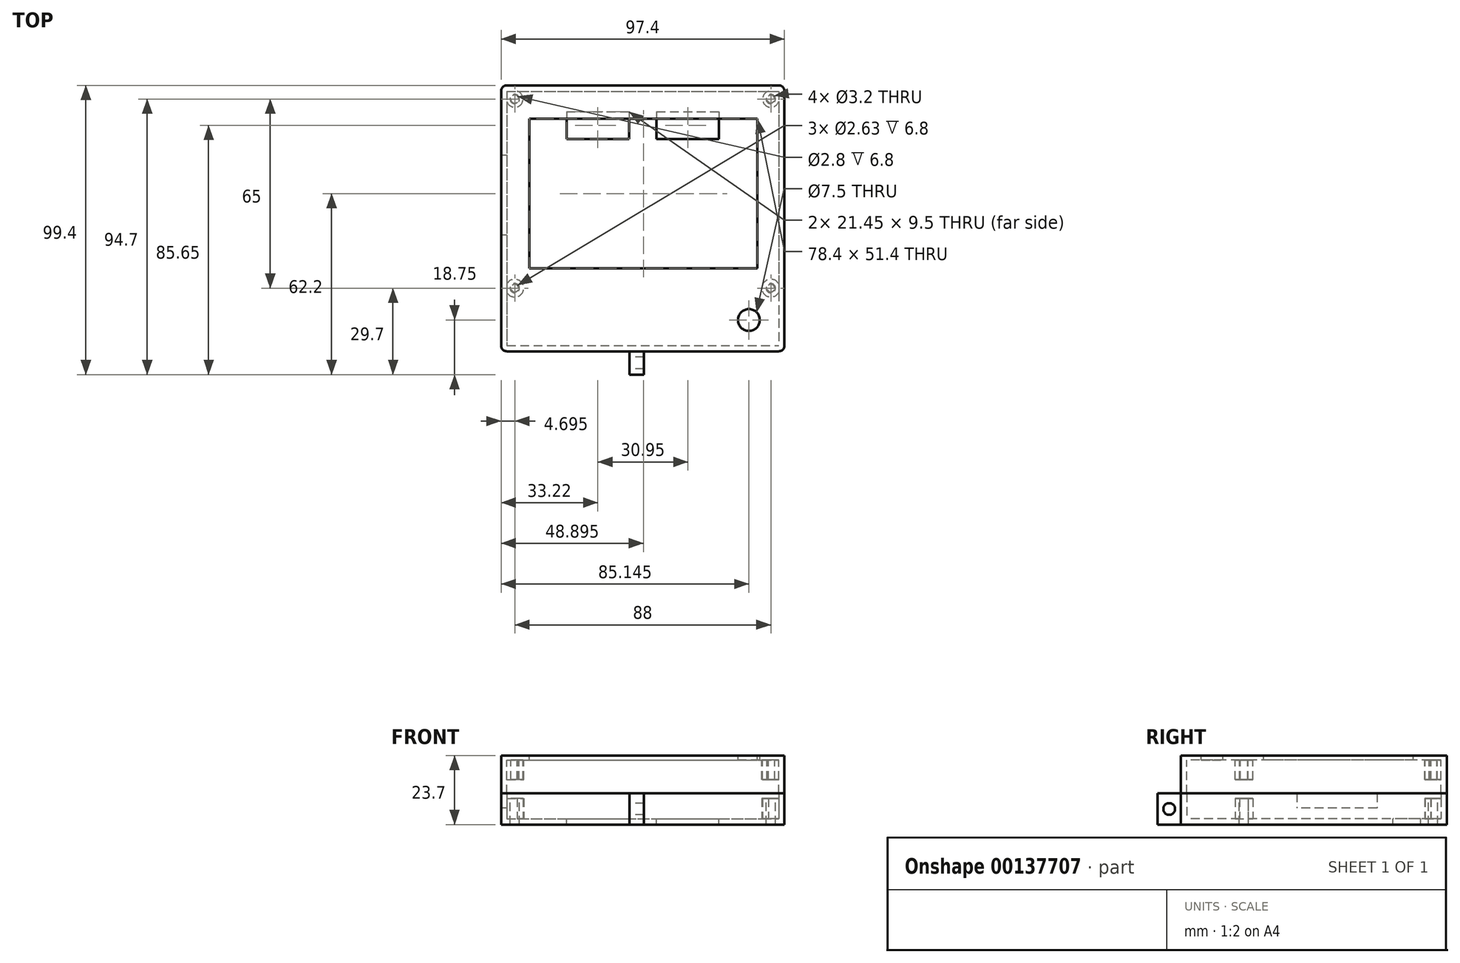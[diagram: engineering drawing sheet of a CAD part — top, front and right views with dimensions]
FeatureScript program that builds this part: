
annotation { "Feature Type Name" : "Feature", "Feature Type Description" : "" }
export const myFeature = defineFeature(function(context is Context, id is Id, definition is map)
    precondition{}
    {
        {
            var Q0;
            Q0=qCreatedBy(makeId("Top.planeOp"),FACE);
            var sketch = newSketch(context, id + "F0", { "sketchPlane" : qUnion([Q0])});
            skLineSegment(sketch, "E0.bottom", {"start": v(-44.61, 43.7) * mm, "end": v(48.79, 43.7) * mm});
            skLineSegment(sketch, "E0.top", {"start": v(-44.61, -43.7) * mm, "end": v(48.79, -43.7) * mm});
            skLineSegment(sketch, "E0.left", {"start": v(-44.61, 43.7) * mm, "end": v(-44.61, -43.7) * mm});
            skLineSegment(sketch, "E0.right", {"start": v(48.79, 43.7) * mm, "end": v(48.79, -43.7) * mm});
            skPoint(sketch, "E0.middle", {"position": v(2.09, 0) * mm});
            skLineSegment(sketch, "E1", {"start": v(-24.11, 36.7) * mm, "end": v(-2.66, 36.7) * mm});
            skLineSegment(sketch, "E2.0", {"start": v(-24.11, 27.2) * mm, "end": v(-2.66, 27.2) * mm});
            skLineSegment(sketch, "E3", {"start": v(-24.11, 36.7) * mm, "end": v(-24.11, 27.2) * mm});
            skLineSegment(sketch, "E4", {"start": v(-2.66, 36.7) * mm, "end": v(-2.66, 27.2) * mm});
            skLineSegment(sketch, "E5", {"start": v(6.84, 36.7) * mm, "end": v(6.84, 27.2) * mm});
            skLineSegment(sketch, "E6", {"start": v(28.29, 36.7) * mm, "end": v(28.29, 27.2) * mm});
            skLineSegment(sketch, "E7.trimOffspring", {"start": v(6.84, 36.7) * mm, "end": v(28.29, 36.7) * mm});
            skLineSegment(sketch, "E8.trimOffspring", {"start": v(6.84, 27.2) * mm, "end": v(28.29, 27.2) * mm});
            skCircle(sketch, "E9", {"center": v(-41.91, 41) * mm, "radius": 1.6 * mm});
            skCircle(sketch, "E10", {"center": v(-41.91, -24) * mm, "radius": 1.6 * mm});
            skCircle(sketch, "E11", {"center": v(46.09, -24) * mm, "radius": 1.6 * mm});
            skCircle(sketch, "E12", {"center": v(46.09, 41) * mm, "radius": 1.6 * mm});
            skLineSegment(sketch, "E13.0", {"start": v(-46.61, 45.7) * mm, "end": v(-46.61, -45.7) * mm});
            skLineSegment(sketch, "E13.1", {"start": v(-46.61, 45.7) * mm, "end": v(50.79, 45.7) * mm});
            skLineSegment(sketch, "E13.2", {"start": v(50.79, 45.7) * mm, "end": v(50.79, -45.7) * mm});
            skLineSegment(sketch, "E13.3", {"start": v(-46.61, -45.7) * mm, "end": v(-2.5, -45.7) * mm});
            skArc(sketch, "E14", {"start": v(-44.61, -25.46) * mm, "mid": v(-38.85, -24) * mm, "end": v(-44.61, -22.54) * mm});
            skArc(sketch, "E15", {"start": v(48.79, -22.54) * mm, "mid": v(43.02, -24) * mm, "end": v(48.79, -25.46) * mm});
            skArc(sketch, "E16.trimOffspring", {"start": v(45.31, 43.7) * mm, "mid": v(44.1, 39.01) * mm, "end": v(48.79, 40.23) * mm});
            skArc(sketch, "E17.trimOffspring", {"start": v(-44.61, 40.15) * mm, "mid": v(-39.91, 39) * mm, "end": v(-41.06, 43.7) * mm});
            skLineSegment(sketch, "E18", {"start": v(0, -61.1) * mm, "end": v(0, -49.71) * mm, "construction": true});
            skLineSegment(sketch, "E19", {"start": v(-2.5, -45.7) * mm, "end": v(-2.5, -53.7) * mm});
            skLineSegment(sketch, "E20", {"start": v(-2.5, -53.7) * mm, "end": v(0, -53.7) * mm});
            skLineSegment(sketch, "E21.MirrorCS", {"start": v(2.5, -53.7) * mm, "end": v(0, -53.7) * mm});
            skLineSegment(sketch, "E22.MirrorCS", {"start": v(2.5, -45.7) * mm, "end": v(2.5, -53.7) * mm});
            skLineSegment(sketch, "E23.trimOffspring", {"start": v(2.5, -45.7) * mm, "end": v(50.79, -45.7) * mm});
            skLineSegment(sketch, "E24", {"start": v(-2.5, -45.7) * mm, "end": v(2.5, -45.7) * mm});
            skSolve(sketch);
        }
        {
            var Q0;
            Q0=makeQuery(id+"F0.imprint","IMPRINT",FACE,{"disambiguationData":[TD([[makeQuery(id+"F0.imprint","IMPRINT",EDGE,{"derivedFrom":sQuery(id+"F0.wireOp",EDGE,"E0.bottom")}),-1.0]])]});
            var Q1;
            Q1=makeQuery(id+"F0.imprint","IMPRINT",FACE,{"disambiguationData":[TD([[makeQuery(id+"F0.imprint","IMPRINT",EDGE,{"derivedFrom":sQuery(id+"F0.wireOp",EDGE,"E0.bottom")}),1.0]])]});
            var Q2;
            {var subQ1=sQuery(id+"F0.wireOp",EDGE,"E0.top");Q2=makeQuery(id+"F0.imprint","IMPRINT",FACE,{"disambiguationData":[TD([[makeQuery(id+"F0.imprint","IMPRINT",EDGE,{"derivedFrom":subQ1}),1.0]])]});}
            var Q3;
            Q3=makeQuery(id+"F0.imprint","IMPRINT",FACE,{"disambiguationData":[TD([[makeQuery(id+"F0.imprint","IMPRINT",EDGE,{"derivedFrom":sQuery(id+"F0.wireOp",EDGE,"E10")}),-1.0]])]});
            var Q4;
            Q4=makeQuery(id+"F0.imprint","IMPRINT",FACE,{"disambiguationData":[TD([[makeQuery(id+"F0.imprint","IMPRINT",EDGE,{"derivedFrom":sQuery(id+"F0.wireOp",EDGE,"E11")}),-1.0]])]});
            var Q5;
            Q5=makeQuery(id+"F0.imprint","IMPRINT",FACE,{"disambiguationData":[TD([[makeQuery(id+"F0.imprint","IMPRINT",EDGE,{"derivedFrom":sQuery(id+"F0.wireOp",EDGE,"E19")}),1.0]])]});
            extrude(context, id + "F1", {"entities" : qUnion([Q0, Q1, Q2, Q3, Q4, Q5]), "oppositeDirection" : true, "depth" : 2 * mm});
        }
        {
            var Q0;
            Q0=makeQuery(id+"F0.imprint","IMPRINT",FACE,{"disambiguationData":[TD([[makeQuery(id+"F0.imprint","IMPRINT",EDGE,{"derivedFrom":sQuery(id+"F0.wireOp",EDGE,"E9")}),-1.0]])]});
            var Q1;
            Q1=makeQuery(id+"F0.imprint","IMPRINT",FACE,{"disambiguationData":[TD([[makeQuery(id+"F0.imprint","IMPRINT",EDGE,{"derivedFrom":sQuery(id+"F0.wireOp",EDGE,"E12")}),-1.0]])]});
            var Q2;
            Q2=makeQuery(id+"F0.imprint","IMPRINT",FACE,{"disambiguationData":[TD([[makeQuery(id+"F0.imprint","IMPRINT",EDGE,{"derivedFrom":sQuery(id+"F0.wireOp",EDGE,"E11")}),-1.0]])]});
            var Q3;
            Q3=makeQuery(id+"F0.imprint","IMPRINT",FACE,{"disambiguationData":[TD([[makeQuery(id+"F0.imprint","IMPRINT",EDGE,{"derivedFrom":sQuery(id+"F0.wireOp",EDGE,"E10")}),-1.0]])]});
            extrude(context, id + "F2", {"entities" : qUnion([Q0, Q1, Q2, Q3]), "operationType" : NewBodyOperationType.ADD, "depth" : 7 * mm});
        }
        {
            var Q0;
            {var subQ1=sQuery(id+"F0.wireOp",EDGE,"E0.top");Q0=makeQuery(id+"F0.imprint","IMPRINT",FACE,{"disambiguationData":[TD([[makeQuery(id+"F0.imprint","IMPRINT",EDGE,{"derivedFrom":subQ1}),-1.0]])]});}
            var Q1;
            Q1=makeQuery(id+"F0.imprint","IMPRINT",FACE,{"disambiguationData":[TD([[makeQuery(id+"F0.imprint","IMPRINT",EDGE,{"derivedFrom":sQuery(id+"F0.wireOp",EDGE,"E19")}),1.0]])]});
            extrude(context, id + "F3", {"entities" : qUnion([Q0, Q1]), "operationType" : NewBodyOperationType.ADD, "depth" : 8.7 * mm});
        }
        {
            var Q0;
            {var subQ0=sQuery(id+"F0.wireOp",EDGE,"E13.0");Q0=makeQuery(id+"F3.boolean.opBoolean","MERGE",FACE,{"derivedFrom":[makeQuery(id+"F1.opExtrude","SWEPT_FACE",FACE,{"disambiguationData":[OSD([subQ0])]}),makeQuery(id+"F3.opExtrude","SWEPT_FACE",FACE,{"disambiguationData":[OSD([subQ0])]})]});}
            var sketch = newSketch(context, id + "F4", { "sketchPlane" : qUnion([Q0])});
            skLineSegment(sketch, "E25.0", {"start": v(-43.7, 8.7) * mm, "end": v(-43.7, 7) * mm, "construction": true});
            skLineSegment(sketch, "E26.0", {"start": v(-43.7, 7) * mm, "end": v(-40.15, 7) * mm, "construction": true});
            skLineSegment(sketch, "E27", {"start": v(-21.7, 3.7) * mm, "end": v(5.8, 3.7) * mm});
            skLineSegment(sketch, "E28", {"start": v(-21.7, 12.56) * mm, "end": v(-21.7, 3.7) * mm});
            skLineSegment(sketch, "E29", {"start": v(5.8, 13.27) * mm, "end": v(5.8, 3.7) * mm});
            skPoint(sketch, "E30.orphan", {"position": v(-21.7, 1.97) * mm});
            skPoint(sketch, "E31.orphan", {"position": v(5.8, 1.97) * mm});
            skSolve(sketch);
        }
        {
            var Q0;
            {var subQ0=sQuery(id+"F4.wireOp",EDGE,"E27");Q0=makeQuery(id+"F4.imprint","IMPRINT",FACE,{"disambiguationData":[TD([[makeQuery(id+"F4.imprint","IMPRINT",EDGE,{"derivedFrom":subQ0}),1.0]])]});}
            extrude(context, id + "F5", {"entities" : qUnion([Q0]), "operationType" : NewBodyOperationType.REMOVE, "endBound" : BoundingType.UP_TO_NEXT, "oppositeDirection" : true, "depth" : 25 * mm});
        }
        {
            var Q0;
            Q0=makeQuery(id+"F3.opExtrude","CAP_FACE",FACE,{"disambiguationData":[OSD([sQuery(id+"F0.wireOp",EDGE,"E0.bottom"),sQuery(id+"F0.wireOp",EDGE,"E0.top"),sQuery(id+"F0.wireOp",EDGE,"E0.left"),sQuery(id+"F0.wireOp",EDGE,"E0.right"),sQuery(id+"F0.wireOp",EDGE,"E13.0"),sQuery(id+"F0.wireOp",EDGE,"E13.1"),sQuery(id+"F0.wireOp",EDGE,"E13.2"),sQuery(id+"F0.wireOp",EDGE,"E13.3")])],"isStart":false});
            cPlane(context, id + "F6", {"entities" : qUnion([Q0]), "cplaneType" : CPlaneType.OFFSET, "offset" : 13 * mm, "width" : 150 * mm, "height" : 150 * mm});
        }
        {
            var Q0;
            Q0=qCreatedBy(id+"F6.planeOp",FACE);
            var sketch = newSketch(context, id + "F7", { "sketchPlane" : qUnion([Q0])});
            skPoint(sketch, "E32.0", {"position": v(46.09, -24) * mm});
            skLineSegment(sketch, "E33.0", {"start": v(-46.61, 45.7) * mm, "end": v(-46.61, -45.7) * mm});
            skLineSegment(sketch, "E34.0", {"start": v(-46.61, 45.7) * mm, "end": v(50.79, 45.7) * mm});
            skLineSegment(sketch, "E35.0", {"start": v(50.79, 45.7) * mm, "end": v(50.79, -45.7) * mm});
            skLineSegment(sketch, "E36.0", {"start": v(-46.61, -45.7) * mm, "end": v(-2.5, -45.7) * mm});
            skLineSegment(sketch, "E37.0", {"start": v(-44.61, 43.7) * mm, "end": v(-44.61, -43.7) * mm});
            skLineSegment(sketch, "E38.0", {"start": v(-44.61, 43.7) * mm, "end": v(48.79, 43.7) * mm});
            skLineSegment(sketch, "E39.0", {"start": v(48.79, 43.7) * mm, "end": v(48.79, -43.7) * mm});
            skLineSegment(sketch, "E40.0", {"start": v(-44.61, -43.7) * mm, "end": v(48.79, -43.7) * mm});
            skArc(sketch, "E41.0", {"start": v(-44.61, 40.15) * mm, "mid": v(-39.91, 39) * mm, "end": v(-41.06, 43.7) * mm});
            skArc(sketch, "E42.0", {"start": v(45.31, 43.7) * mm, "mid": v(44.1, 39.01) * mm, "end": v(48.79, 40.23) * mm});
            skArc(sketch, "E43.0", {"start": v(-44.61, -25.46) * mm, "mid": v(-38.85, -24) * mm, "end": v(-44.61, -22.54) * mm});
            skArc(sketch, "E44.0", {"start": v(48.79, -22.54) * mm, "mid": v(43.02, -24) * mm, "end": v(48.79, -25.46) * mm});
            skLineSegment(sketch, "E45.bottom", {"start": v(-36.91, 34.2) * mm, "end": v(41.49, 34.2) * mm});
            skLineSegment(sketch, "E45.top", {"start": v(-36.91, -17.2) * mm, "end": v(41.49, -17.2) * mm});
            skLineSegment(sketch, "E45.left", {"start": v(-36.91, 34.2) * mm, "end": v(-36.91, -17.2) * mm});
            skLineSegment(sketch, "E45.right", {"start": v(41.49, 34.2) * mm, "end": v(41.49, -17.2) * mm});
            skCircle(sketch, "E46", {"center": v(-41.91, 41) * mm, "radius": 1.4 * mm});
            skCircle(sketch, "E47", {"center": v(46.09, 41) * mm, "radius": 1.31 * mm});
            skCircle(sketch, "E48", {"center": v(-41.91, -24) * mm, "radius": 1.31 * mm});
            skCircle(sketch, "E49", {"center": v(46.09, -24) * mm, "radius": 1.31 * mm});
            skCircle(sketch, "E50", {"center": v(38.54, -34.95) * mm, "radius": 3.75 * mm});
            skLineSegment(sketch, "E51.0", {"start": v(2.5, -45.7) * mm, "end": v(50.79, -45.7) * mm});
            skLineSegment(sketch, "E52.0", {"start": v(-2.5, -45.7) * mm, "end": v(2.5, -45.7) * mm});
            skSolve(sketch);
        }
        {
            var Q0;
            Q0=makeQuery(id+"F7.imprint","IMPRINT",FACE,{"disambiguationData":[TD([[makeQuery(id+"F7.imprint","IMPRINT",EDGE,{"derivedFrom":sQuery(id+"F7.wireOp",EDGE,"E33.0")}),1.0]])]});
            extrude(context, id + "F8", {"entities" : qUnion([Q0]), "oppositeDirection" : true, "depth" : 13 * mm});
        }
        {
            var Q0;
            {var subQ3=sQuery(id+"F7.wireOp",EDGE,"E41.0");Q0=makeQuery(id+"F7.imprint","IMPRINT",FACE,{"disambiguationData":[TD([[makeQuery(id+"F7.imprint","IMPRINT",EDGE,{"derivedFrom":subQ3}),1.0]])]});}
            var Q1;
            {var subQ3=sQuery(id+"F7.wireOp",EDGE,"E42.0");Q1=makeQuery(id+"F7.imprint","IMPRINT",FACE,{"disambiguationData":[TD([[makeQuery(id+"F7.imprint","IMPRINT",EDGE,{"derivedFrom":subQ3}),1.0]])]});}
            var Q2;
            {var subQ0=sQuery(id+"F7.wireOp",EDGE,"E44.0");Q2=makeQuery(id+"F7.imprint","IMPRINT",FACE,{"disambiguationData":[TD([[makeQuery(id+"F7.imprint","IMPRINT",EDGE,{"derivedFrom":subQ0}),1.0]])]});}
            var Q3;
            {var subQ0=sQuery(id+"F7.wireOp",EDGE,"E43.0");Q3=makeQuery(id+"F7.imprint","IMPRINT",FACE,{"disambiguationData":[TD([[makeQuery(id+"F7.imprint","IMPRINT",EDGE,{"derivedFrom":subQ0}),1.0]])]});}
            extrude(context, id + "F9", {"entities" : qUnion([Q0, Q1, Q2, Q3]), "operationType" : NewBodyOperationType.ADD, "oppositeDirection" : true, "depth" : 8.3 * mm});
        }
        {
            var Q0;
            {var subQ2=sQuery(id+"F7.wireOp",EDGE,"E40.0");Q0=makeQuery(id+"F7.imprint","IMPRINT",FACE,{"disambiguationData":[TD([[makeQuery(id+"F7.imprint","IMPRINT",EDGE,{"derivedFrom":subQ2}),1.0]])]});}
            var Q1;
            Q1=makeQuery(id+"F7.imprint","IMPRINT",FACE,{"disambiguationData":[TD([[makeQuery(id+"F7.imprint","IMPRINT",EDGE,{"derivedFrom":sQuery(id+"F7.wireOp",EDGE,"E46")}),1.0]])]});
            var Q2;
            Q2=makeQuery(id+"F7.imprint","IMPRINT",FACE,{"disambiguationData":[TD([[makeQuery(id+"F7.imprint","IMPRINT",EDGE,{"derivedFrom":sQuery(id+"F7.wireOp",EDGE,"E48")}),1.0]])]});
            var Q3;
            Q3=makeQuery(id+"F7.imprint","IMPRINT",FACE,{"disambiguationData":[TD([[makeQuery(id+"F7.imprint","IMPRINT",EDGE,{"derivedFrom":sQuery(id+"F7.wireOp",EDGE,"E47")}),1.0]])]});
            var Q4;
            Q4=makeQuery(id+"F7.imprint","IMPRINT",FACE,{"disambiguationData":[TD([[makeQuery(id+"F7.imprint","IMPRINT",EDGE,{"derivedFrom":sQuery(id+"F7.wireOp",EDGE,"E49")}),1.0]])]});
            extrude(context, id + "F10", {"entities" : qUnion([Q0, Q1, Q2, Q3, Q4]), "operationType" : NewBodyOperationType.ADD, "oppositeDirection" : true, "depth" : 1.5 * mm});
        }
        {
            var Q0;
            {var subQ0=sQuery(id+"F0.wireOp",EDGE,"E19");Q0=makeQuery(id+"F3.boolean.opBoolean","MERGE",FACE,{"derivedFrom":[makeQuery(id+"F1.opExtrude","SWEPT_FACE",FACE,{"disambiguationData":[OSD([subQ0])]}),makeQuery(id+"F3.opExtrude","SWEPT_FACE",FACE,{"disambiguationData":[OSD([subQ0])]})]});}
            var sketch = newSketch(context, id + "F11", { "sketchPlane" : qUnion([Q0])});
            skCircle(sketch, "E53", {"center": v(49.7, 3.35) * mm, "radius": 2 * mm});
            skPoint(sketch, "E53.centerSnap0", {"position": v(53.7, 3.35) * mm});
            skPoint(sketch, "E53.centerSnap1", {"position": v(49.7, 8.7) * mm});
            skSolve(sketch);
        }
        {
            var Q0;
            Q0=makeQuery(id+"F11.imprint","IMPRINT",FACE,{"disambiguationData":[TD([[makeQuery(id+"F11.imprint","IMPRINT",EDGE,{"derivedFrom":sQuery(id+"F11.wireOp",EDGE,"E53")}),1.0]])]});
            extrude(context, id + "F12", {"entities" : qUnion([Q0]), "operationType" : NewBodyOperationType.REMOVE, "endBound" : BoundingType.THROUGH_ALL, "oppositeDirection" : true, "depth" : 25 * mm});
        }
        {
            var Q0;
            Q0=makeQuery(id+"F8.opExtrude","SWEPT_EDGE",EDGE,{"disambiguationData":[OSD([sQuery(id+"F7.wireOp",EDGE,"E33.0"),sQuery(id+"F7.wireOp",EDGE,"E36.0")])]});
            var Q1;
            {var subQ0=sQuery(id+"F0.wireOp",EDGE,"E13.3");var subQ1=sQuery(id+"F0.wireOp",EDGE,"E13.0");Q1=makeQuery(id+"F3.boolean.opBoolean","MERGE",EDGE,{"derivedFrom":[makeQuery(id+"F1.opExtrude","SWEPT_EDGE",EDGE,{"disambiguationData":[OSD([subQ1,subQ0])]}),makeQuery(id+"F3.opExtrude","SWEPT_EDGE",EDGE,{"disambiguationData":[OSD([subQ1,subQ0])]})]});}
            var Q2;
            Q2=makeQuery(id+"F8.opExtrude","SWEPT_EDGE",EDGE,{"disambiguationData":[OSD([sQuery(id+"F7.wireOp",EDGE,"E35.0"),sQuery(id+"F7.wireOp",EDGE,"E51.0")])]});
            var Q3;
            {var subQ0=sQuery(id+"F0.wireOp",EDGE,"E23.trimOffspring");var subQ1=sQuery(id+"F0.wireOp",EDGE,"E13.2");Q3=makeQuery(id+"F3.boolean.opBoolean","MERGE",EDGE,{"derivedFrom":[makeQuery(id+"F1.opExtrude","SWEPT_EDGE",EDGE,{"disambiguationData":[OSD([subQ1,subQ0])]}),makeQuery(id+"F3.opExtrude","SWEPT_EDGE",EDGE,{"disambiguationData":[OSD([subQ1,subQ0])]})]});}
            var Q4;
            Q4=makeQuery(id+"F8.opExtrude","SWEPT_EDGE",EDGE,{"disambiguationData":[OSD([sQuery(id+"F7.wireOp",EDGE,"E34.0"),sQuery(id+"F7.wireOp",EDGE,"E35.0")])]});
            var Q5;
            {var subQ0=sQuery(id+"F0.wireOp",EDGE,"E13.2");var subQ1=sQuery(id+"F0.wireOp",EDGE,"E13.1");Q5=makeQuery(id+"F3.boolean.opBoolean","MERGE",EDGE,{"derivedFrom":[makeQuery(id+"F1.opExtrude","SWEPT_EDGE",EDGE,{"disambiguationData":[OSD([subQ1,subQ0])]}),makeQuery(id+"F3.opExtrude","SWEPT_EDGE",EDGE,{"disambiguationData":[OSD([subQ1,subQ0])]})]});}
            var Q6;
            Q6=makeQuery(id+"F8.opExtrude","SWEPT_EDGE",EDGE,{"disambiguationData":[OSD([sQuery(id+"F7.wireOp",EDGE,"E33.0"),sQuery(id+"F7.wireOp",EDGE,"E34.0")])]});
            var Q7;
            {var subQ0=sQuery(id+"F0.wireOp",EDGE,"E13.1");var subQ1=sQuery(id+"F0.wireOp",EDGE,"E13.0");Q7=makeQuery(id+"F3.boolean.opBoolean","MERGE",EDGE,{"derivedFrom":[makeQuery(id+"F1.opExtrude","SWEPT_EDGE",EDGE,{"disambiguationData":[OSD([subQ1,subQ0])]}),makeQuery(id+"F3.opExtrude","SWEPT_EDGE",EDGE,{"disambiguationData":[OSD([subQ1,subQ0])]})]});}
            fillet(context, id + "F13", {"entities" : qUnion([Q0, Q1, Q2, Q3, Q4, Q5, Q6, Q7]), "radius" : 2 * mm, "tangentPropagation" : true, "allowEdgeOverflow" : false});
        }
    });
